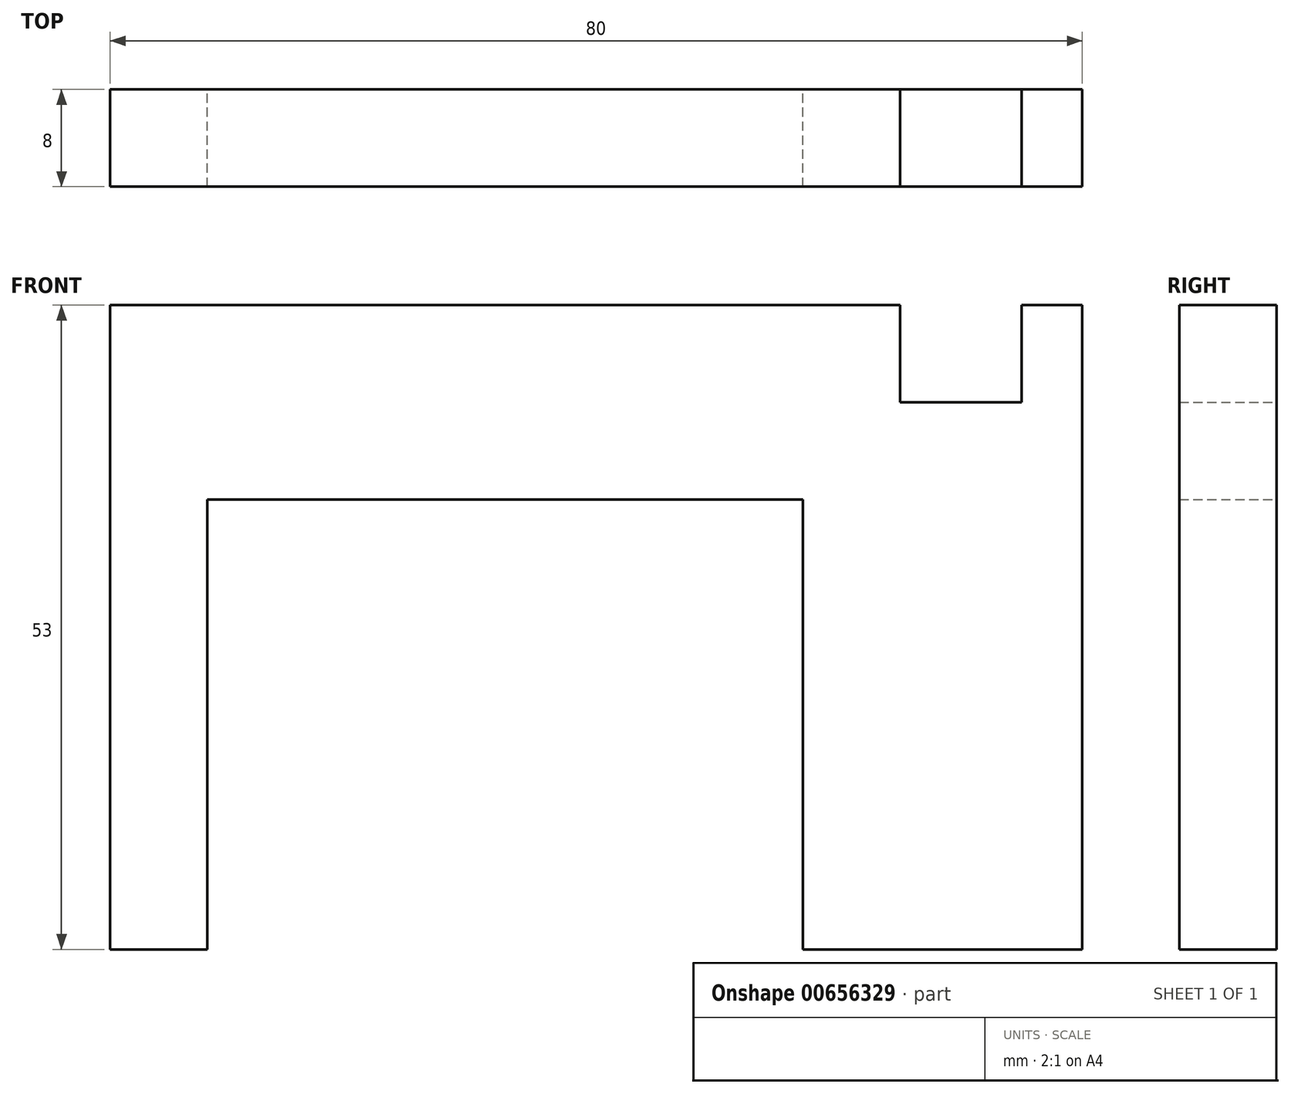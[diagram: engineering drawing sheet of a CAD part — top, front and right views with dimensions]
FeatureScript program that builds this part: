
annotation { "Feature Type Name" : "Feature", "Feature Type Description" : "" }
export const myFeature = defineFeature(function(context is Context, id is Id, definition is map)
    precondition{}
    {
        {
            var Q0;
            Q0=qCreatedBy(makeId("Front.planeOp"),FACE);
            var sketch = newSketch(context, id + "F0", { "sketchPlane" : qUnion([Q0])});
            skLineSegment(sketch, "E0.bottom", {"start": v(40, 26.5) * mm, "end": v(-40, 26.5) * mm});
            skLineSegment(sketch, "E0.top", {"start": v(40, -26.5) * mm, "end": v(-40, -26.5) * mm});
            skLineSegment(sketch, "E0.left", {"start": v(40, 26.5) * mm, "end": v(40, -26.5) * mm});
            skLineSegment(sketch, "E0.right", {"start": v(-40, 26.5) * mm, "end": v(-40, -26.5) * mm});
            skPoint(sketch, "E0.middle", {"position": v(0, 0) * mm});
            skLineSegment(sketch, "E1.bottom", {"start": v(35, 26.5) * mm, "end": v(25, 26.5) * mm});
            skLineSegment(sketch, "E1.top", {"start": v(35, 18.5) * mm, "end": v(25, 18.5) * mm});
            skLineSegment(sketch, "E1.left", {"start": v(35, 26.5) * mm, "end": v(35, 18.5) * mm});
            skLineSegment(sketch, "E1.right", {"start": v(25, 26.5) * mm, "end": v(25, 18.5) * mm});
            skLineSegment(sketch, "E2.bottom", {"start": v(-32, -26.5) * mm, "end": v(17, -26.5) * mm});
            skLineSegment(sketch, "E2.top", {"start": v(-32, 10.5) * mm, "end": v(17, 10.5) * mm});
            skLineSegment(sketch, "E2.left", {"start": v(-32, -26.5) * mm, "end": v(-32, 10.5) * mm});
            skLineSegment(sketch, "E2.right", {"start": v(17, -26.5) * mm, "end": v(17, 10.5) * mm});
            skSolve(sketch);
        }
        {
            var Q0;
            {var subQ3=sQuery(id+"F0.wireOp",EDGE,"E0.left");Q0=makeQuery(id+"F0.imprint","IMPRINT",FACE,{"disambiguationData":[TD([[makeQuery(id+"F0.imprint","IMPRINT",EDGE,{"derivedFrom":subQ3}),-1.0]])]});}
            extrude(context, id + "F1", {"entities" : qUnion([Q0]), "depth" : 8 * mm, "offsetDistance" : 25 * mm});
        }
    });
